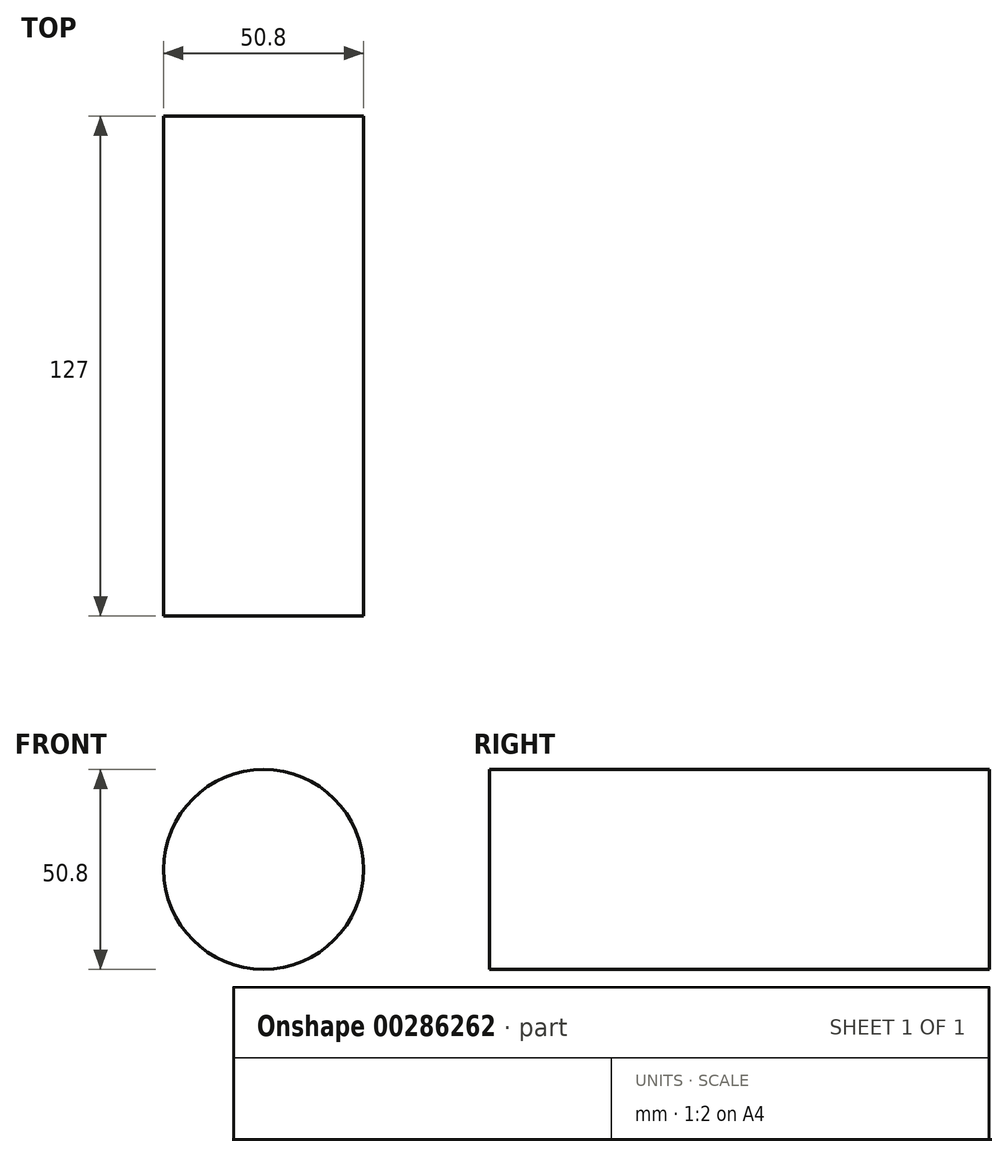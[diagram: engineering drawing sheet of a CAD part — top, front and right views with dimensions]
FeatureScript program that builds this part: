
annotation { "Feature Type Name" : "Feature", "Feature Type Description" : "" }
export const myFeature = defineFeature(function(context is Context, id is Id, definition is map)
    precondition{}
    {
        {
            var Q0;
            Q0=qCreatedBy(makeId("Front.planeOp"),FACE);
            var sketch = newSketch(context, id + "F0", { "sketchPlane" : qUnion([Q0])});
            skCircle(sketch, "E0", {"center": v(0, 0) * mm, "radius": 25.4 * mm});
            skSolve(sketch);
        }
        {
            var Q0;
            Q0=sQuery(id+"F0.wireOp",EDGE,"E0");
            extrude(context, id + "F1", {"bodyType" : ToolBodyType.SURFACE, "surfaceEntities" : qUnion([Q0]), "depth" : 127 * mm});
        }
    });
